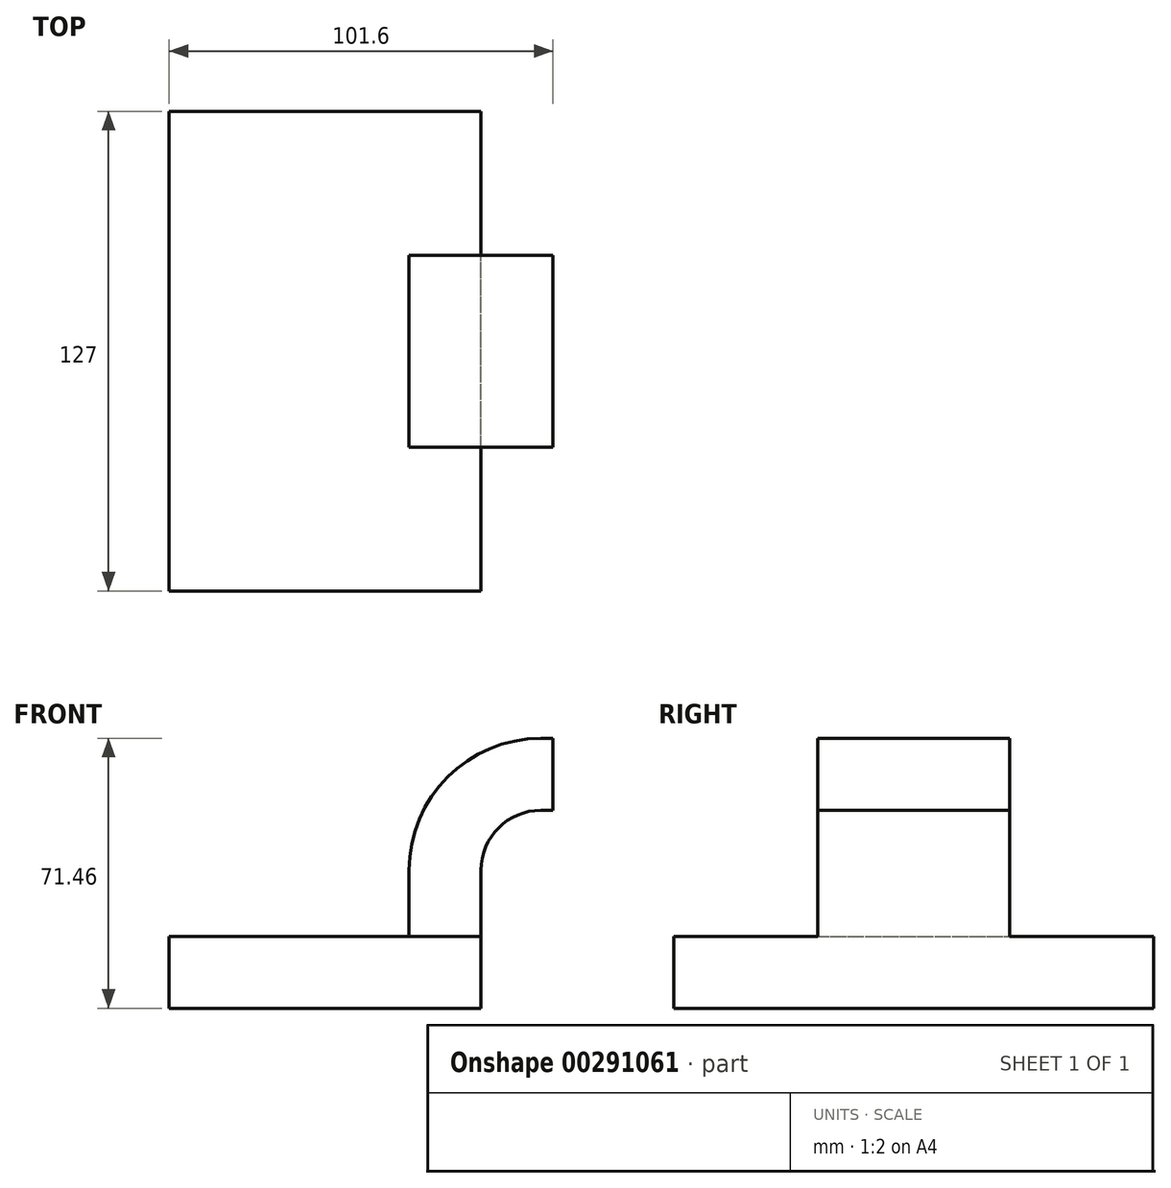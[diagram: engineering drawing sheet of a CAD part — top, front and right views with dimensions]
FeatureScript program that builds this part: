
annotation { "Feature Type Name" : "Feature", "Feature Type Description" : "" }
export const myFeature = defineFeature(function(context is Context, id is Id, definition is map)
    precondition{}
    {
        {
            var Q0;
            Q0=qCreatedBy(makeId("Front.planeOp"),FACE);
            var sketch = newSketch(context, id + "F0", { "sketchPlane" : qUnion([Q0])});
            skLineSegment(sketch, "E0.bottom", {"start": v(41.28, -9.52) * mm, "end": v(-41.28, -9.53) * mm});
            skLineSegment(sketch, "E0.top", {"start": v(41.28, 9.53) * mm, "end": v(-41.28, 9.53) * mm});
            skLineSegment(sketch, "E0.left", {"start": v(41.28, -9.52) * mm, "end": v(41.28, 9.53) * mm});
            skLineSegment(sketch, "E0.right", {"start": v(-41.28, -9.53) * mm, "end": v(-41.28, 9.52) * mm});
            skPoint(sketch, "E0.middle", {"position": v(0, 0) * mm});
            skLineSegment(sketch, "E1.bottom", {"start": v(60.32, 38.1) * mm, "end": v(111.12, 38.1) * mm});
            skLineSegment(sketch, "E1.top", {"start": v(60.32, 66.68) * mm, "end": v(111.12, 66.68) * mm});
            skLineSegment(sketch, "E1.left", {"start": v(60.32, 38.1) * mm, "end": v(60.32, 66.68) * mm});
            skLineSegment(sketch, "E1.right", {"start": v(111.12, 38.1) * mm, "end": v(111.12, 66.68) * mm});
            skPoint(sketch, "E1.middle", {"position": v(85.72, 52.39) * mm});
            skLineSegment(sketch, "E2", {"start": v(41.28, 9.53) * mm, "end": v(41.28, 27) * mm});
            skArc(sketch, "E3", {"start": v(41.28, 27) * mm, "mid": v(45.92, 38.23) * mm, "end": v(57.15, 42.88) * mm});
            skLineSegment(sketch, "E4", {"start": v(57.15, 42.88) * mm, "end": v(85.72, 42.88) * mm});
            skLineSegment(sketch, "E5.0", {"start": v(57.15, 61.93) * mm, "end": v(85.72, 61.93) * mm});
            skArc(sketch, "E5.1", {"start": v(22.23, 27) * mm, "mid": v(32.45, 51.7) * mm, "end": v(57.15, 61.93) * mm});
            skLineSegment(sketch, "E5.2", {"start": v(22.23, 9.53) * mm, "end": v(22.23, 27) * mm});
            skLineSegment(sketch, "E6", {"start": v(85.72, 38.1) * mm, "end": v(85.72, 66.68) * mm});
            skFitSpline(sketch, "E7", {"points": [v(-41.28, 9.52) * mm, v(57.15, 61.93) * mm], "startDerivative": vector(-4.25, 110.1) * mm, "endDerivative": vector(185.88, -2.23) * mm});
            skSolve(sketch);
        }
        {
            var Q0;
            Q0=makeQuery(id+"F0.imprint","IMPRINT",FACE,{"disambiguationData":[TD([[makeQuery(id+"F0.imprint","IMPRINT",EDGE,{"derivedFrom":sQuery(id+"F0.wireOp",EDGE,"E0.bottom")}),-1.0]])]});
            extrude(context, id + "F1", {"entities" : qUnion([Q0]), "endBound" : BoundingType.SYMMETRIC, "depth" : 127 * mm});
        }
        {
            var Q0;
            {var subQ1=sQuery(id+"F0.wireOp",EDGE,"E2");Q0=makeQuery(id+"F0.imprint","IMPRINT",FACE,{"disambiguationData":[TD([[makeQuery(id+"F0.imprint","IMPRINT",EDGE,{"derivedFrom":subQ1}),1.0]])]});}
            extrude(context, id + "F2", {"entities" : qUnion([Q0]), "operationType" : NewBodyOperationType.ADD, "endBound" : BoundingType.SYMMETRIC, "depth" : 50.8 * mm});
        }
        {
            var Q0;
            Q0=makeQuery(id+"F0.imprint","IMPRINT",FACE,{"disambiguationData":[TD([[makeQuery(id+"F0.imprint","IMPRINT",EDGE,{"derivedFrom":sQuery(id+"F0.wireOp",EDGE,"E5.1")}),1.0]])]});
            extrude(context, id + "F3", {"entities" : qUnion([Q0]), "operationType" : NewBodyOperationType.ADD, "endBound" : BoundingType.SYMMETRIC, "depth" : 15.88 * mm});
        }
    });
